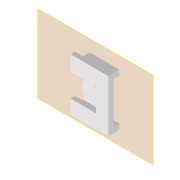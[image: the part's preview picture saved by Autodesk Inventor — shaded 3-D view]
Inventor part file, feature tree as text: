
AUTODESK INVENTOR PART (.ipt)
format: ipt  version: 2022 (Build 260153000, 153)  size: 164,352 bytes
history: native  units: in
note: dims shown in document units (in); Inventor stores cm internally (conversion verified against a paired STEP export)
features: sketch x5, extrude x5, other x5, reference x3, projected_geometry x3, plane x2
ambient origin geometry x8: Origin, YZ Plane, XZ Plane, XY Plane, X Axis, Y Axis, Z Axis, Center Point
bodies: Volumenkörper1 (feature_tree)
feature tree (23):
  plane  "Arbeitsebene1"
  sketch  "Skizze1"  dims[d0=0.0in d1=0.0197in]
  plane  "Arbeitsebene2"
  extrude  "Extrusion1"  Depth=0.0197in
  extrude  "Extrusion2"  Depth=0.0787in
  extrude  "Extrusion3"  Depth=0.3937in
  extrude  "Extrusion4"  TaperAngle=0.0deg  [1 undecoded]
  extrude  "Extrusion5"  Depth=0.3465in
  reference  "Referenz1"
  reference  "Referenz2"
  sketch  "Skizze2"  dims[d2=0.0197in d3=0.0787in]
  projected_geometry  "Projizierte Kontur1"
  sketch  "Skizze3"  dims[d4=0.0787in d5=0.3937in]
  projected_geometry  "Projizierte Kontur2"
  sketch  "Skizze4"  dims[d6=0.0197in d7=0.0in]
  projected_geometry  "Projizierte Kontur3"
  sketch  "Skizze5"  dims[d8=0.3465in d9=0.3465in d10=0.0787in d11=0.0in d12=0.1181in d13=0.0984in d14=0.0in d15=0.0787in d16=0.0in d17=0.0039in d18=0.0in]
  reference  "Referenz3"
  other  "00_ESP3-CAM.iam"
  other  "Bauteil50"
  other  "MicroSD Slot v1:1"
  other  "sdreader:1"
  other  "<userpath>\Documents\GitHub\Matchboxscope\INVENTOR\00_ESP3-CAM.iam"
note: 1 required parameter value undecoded (feature->parameter linkage not recoverable at this tier; creation-order binding heuristic only, values carry confidence <= 0.55)
